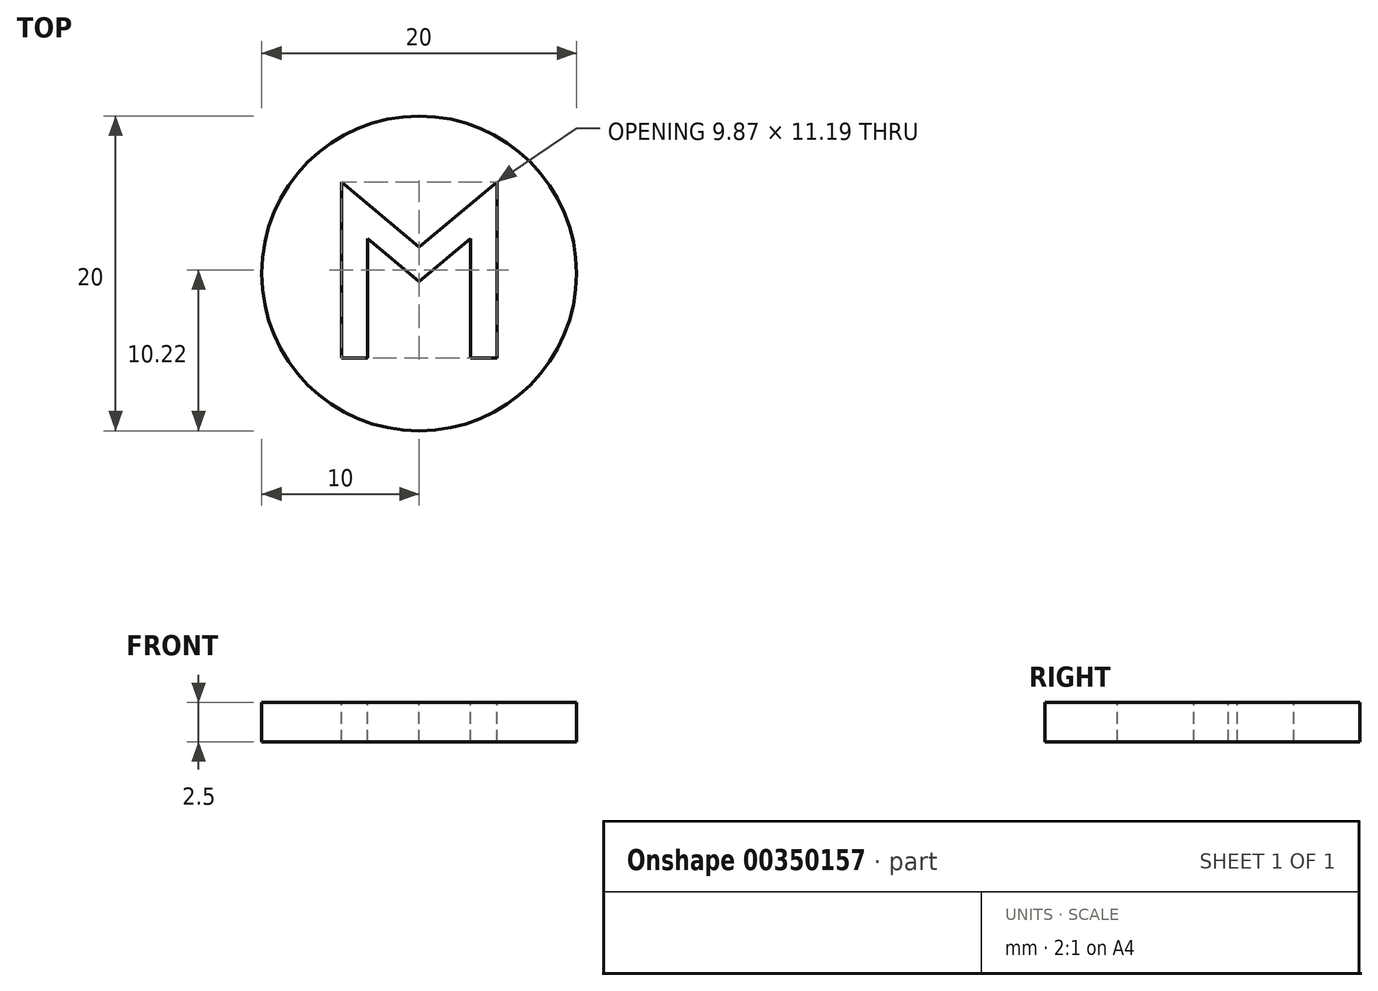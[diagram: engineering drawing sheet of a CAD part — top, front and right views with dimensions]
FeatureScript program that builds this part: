
annotation { "Feature Type Name" : "Feature", "Feature Type Description" : "" }
export const myFeature = defineFeature(function(context is Context, id is Id, definition is map)
    precondition{}
    {
        {
            var Q0;
            Q0=qCreatedBy(makeId("Top.planeOp"),FACE);
            var sketch = newSketch(context, id + "F0", { "sketchPlane" : qUnion([Q0])});
            skCircle(sketch, "E0", {"center": v(0, 0) * mm, "radius": 10 * mm});
            skSolve(sketch);
        }
        {
            var Q0;
            Q0 = qSketchRegion(id + "F0", true);
            extrude(context, id + "F1", {"entities" : qUnion([Q0]), "depth" : 2.5 * mm});
        }
        {
            var Q0;
            Q0=makeQuery(id+"F1.opExtrude","CAP_FACE",FACE,{"disambiguationData":[OSD([sQuery(id+"F0.wireOp",EDGE,"E0")])],"isStart":false});
            var sketch = newSketch(context, id + "F2", { "sketchPlane" : qUnion([Q0])});
            skLineSegment(sketch, "E1", {"start": v(0, 1.67) * mm, "end": v(4.94, 5.81) * mm});
            skLineSegment(sketch, "E2", {"start": v(4.94, 5.81) * mm, "end": v(4.94, -5.37) * mm});
            skLineSegment(sketch, "E3", {"start": v(4.94, -5.37) * mm, "end": v(3.26, -5.37) * mm});
            skLineSegment(sketch, "E4", {"start": v(3.26, -5.37) * mm, "end": v(3.26, 2.22) * mm});
            skLineSegment(sketch, "E5", {"start": v(3.26, 2.22) * mm, "end": v(0, -0.52) * mm});
            skLineSegment(sketch, "E6", {"start": v(0, -0.52) * mm, "end": v(0, 0) * mm, "construction": true});
            skLineSegment(sketch, "E7", {"start": v(3.26, 2.22) * mm, "end": v(2.18, 3.5) * mm, "construction": true});
            skLineSegment(sketch, "E8.MirrorCS", {"start": v(-3.26, 2.22) * mm, "end": v(-2.18, 3.5) * mm, "construction": true});
            skLineSegment(sketch, "E9.MirrorCS", {"start": v(-3.26, 2.22) * mm, "end": v(0, -0.52) * mm});
            skLineSegment(sketch, "E10.MirrorCS", {"start": v(-3.26, -5.37) * mm, "end": v(-3.26, 2.22) * mm});
            skLineSegment(sketch, "E11.MirrorCS", {"start": v(0, 1.67) * mm, "end": v(-4.94, 5.81) * mm});
            skLineSegment(sketch, "E12.MirrorCS", {"start": v(-4.94, -5.37) * mm, "end": v(-3.26, -5.37) * mm});
            skLineSegment(sketch, "E13.MirrorCS", {"start": v(-4.94, 5.81) * mm, "end": v(-4.94, -5.37) * mm});
            skSolve(sketch);
        }
        {
            var Q0;
            Q0 = qSketchRegion(id + "F2", true);
            extrude(context, id + "F3", {"entities" : qUnion([Q0]), "operationType" : NewBodyOperationType.REMOVE, "endBound" : BoundingType.THROUGH_ALL, "oppositeDirection" : true, "depth" : 25 * mm});
        }
    });
